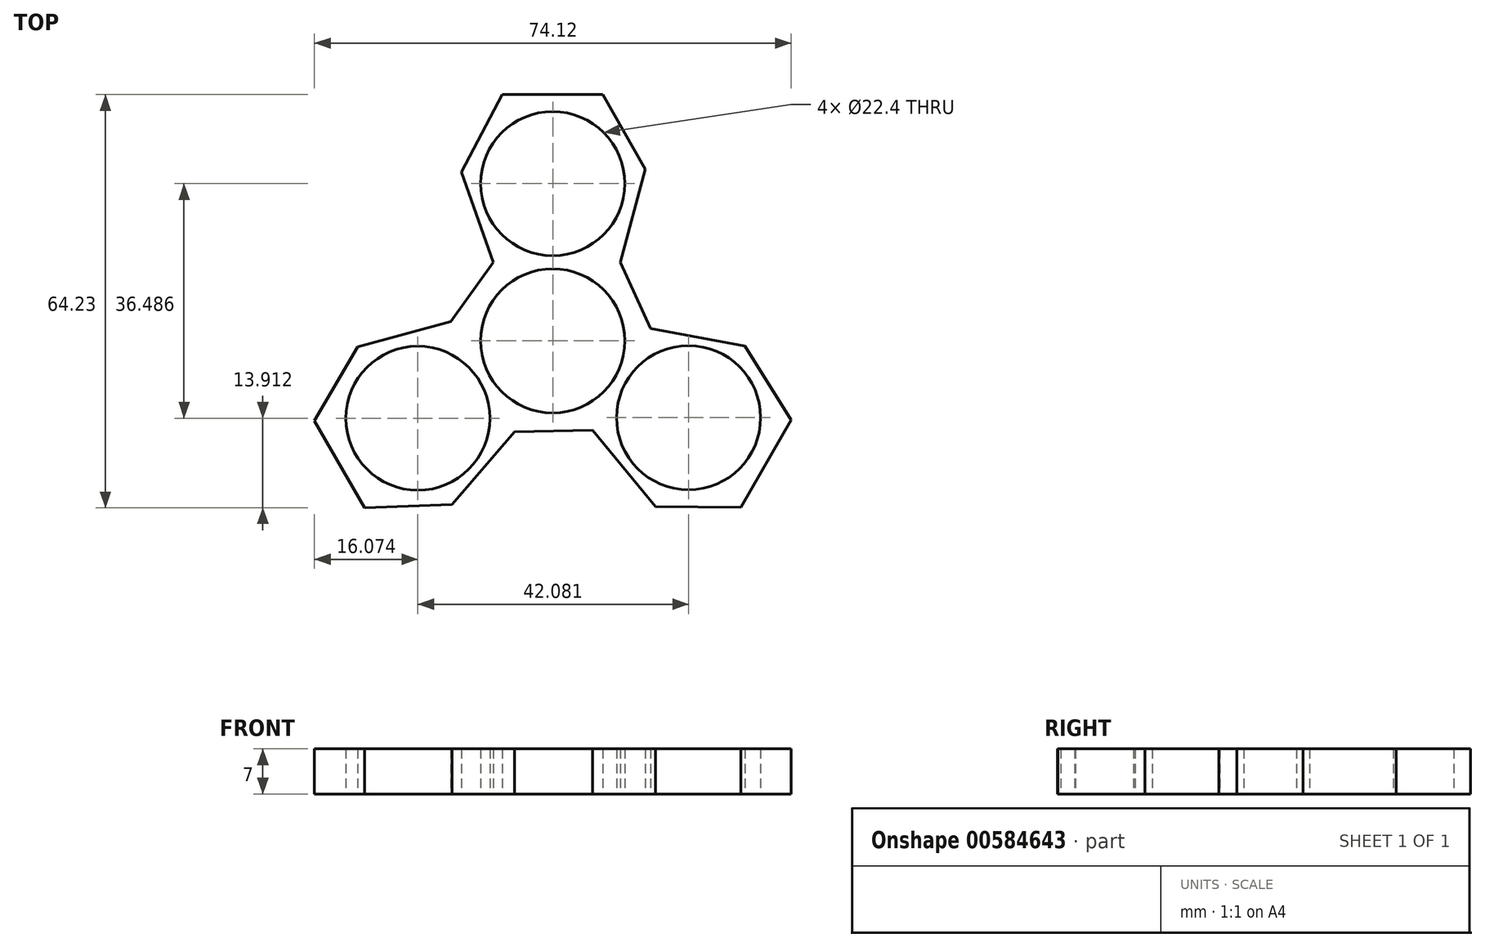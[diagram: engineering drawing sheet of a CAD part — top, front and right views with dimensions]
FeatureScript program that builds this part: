
annotation { "Feature Type Name" : "Feature", "Feature Type Description" : "" }
export const myFeature = defineFeature(function(context is Context, id is Id, definition is map)
    precondition{}
    {
        {
            var Q0;
            Q0=qCreatedBy(makeId("Top.planeOp"),FACE);
            var sketch = newSketch(context, id + "F0", { "sketchPlane" : qUnion([Q0])});
            skPoint(sketch, "E0.center", {"position": v(0, 0) * mm});
            skPoint(sketch, "E1.orphan", {"position": v(-15.95, 24.45) * mm});
            skPoint(sketch, "E2.2.0.center.orphan", {"position": v(0, 24.45) * mm});
            skPoint(sketch, "E3.orphan", {"position": v(15.54, 24.45) * mm});
            skCircle(sketch, "E4", {"center": v(0, 0) * mm, "radius": 11.2 * mm});
            skCircle(sketch, "E5", {"center": v(0, 24.45) * mm, "radius": 11.2 * mm});
            skCircle(sketch, "E6.1.0", {"center": v(-20.97, -12.04) * mm, "radius": 11.2 * mm});
            skCircle(sketch, "E6.2.0", {"center": v(21.12, -11.95) * mm, "radius": 11.2 * mm});
            skPoint(sketch, "E6.center", {"position": v(0.05, 0.15) * mm});
            skLineSegment(sketch, "E7", {"start": v(-7.86, 38.28) * mm, "end": v(7.78, 38.28) * mm});
            skLineSegment(sketch, "E8", {"start": v(7.78, 38.28) * mm, "end": v(14.35, 26.72) * mm});
            skLineSegment(sketch, "E9", {"start": v(14.35, 26.72) * mm, "end": v(10.5, 12.2) * mm});
            skLineSegment(sketch, "E10", {"start": v(-7.86, 38.28) * mm, "end": v(-14.21, 26.26) * mm});
            skLineSegment(sketch, "E11", {"start": v(-14.21, 26.26) * mm, "end": v(-9.26, 12.2) * mm});
            skLineSegment(sketch, "E12.1.0", {"start": v(29.85, -0.82) * mm, "end": v(15.2, 1.92) * mm});
            skLineSegment(sketch, "E12.1.2", {"start": v(29.26, -25.87) * mm, "end": v(15.96, -25.79) * mm});
            skLineSegment(sketch, "E12.1.3", {"start": v(37.08, -12.33) * mm, "end": v(29.26, -25.87) * mm});
            skLineSegment(sketch, "E12.1.4", {"start": v(37.08, -12.33) * mm, "end": v(29.85, -0.82) * mm});
            skLineSegment(sketch, "E12.2.0", {"start": v(-15.64, -25.44) * mm, "end": v(-5.94, -14.12) * mm});
            skLineSegment(sketch, "E12.2.1", {"start": v(-30.31, -0.93) * mm, "end": v(-15.82, 2.99) * mm});
            skLineSegment(sketch, "E12.2.2", {"start": v(-37.04, -12.4) * mm, "end": v(-30.31, -0.93) * mm});
            skLineSegment(sketch, "E12.2.3", {"start": v(-29.22, -25.95) * mm, "end": v(-37.04, -12.4) * mm});
            skLineSegment(sketch, "E12.2.4", {"start": v(-29.22, -25.95) * mm, "end": v(-15.64, -25.44) * mm});
            skLineSegment(sketch, "E12.anchor1", {"start": v(0, 0) * mm, "end": v(-9.26, 12.2) * mm, "construction": true});
            skLineSegment(sketch, "E13", {"start": v(-15.82, 2.99) * mm, "end": v(-9.26, 12.2) * mm});
            skLineSegment(sketch, "E14", {"start": v(15.96, -25.79) * mm, "end": v(6.2, -13.86) * mm});
            skLineSegment(sketch, "E15", {"start": v(-5.94, -14.12) * mm, "end": v(6.2, -13.86) * mm});
            skLineSegment(sketch, "E16", {"start": v(10.5, 12.2) * mm, "end": v(15.2, 1.92) * mm});
            skSolve(sketch);
        }
        {
            var Q0;
            Q0 = qSketchRegion(id + "F0", true);
            extrude(context, id + "F1", {"entities" : qUnion([Q0]), "depth" : 7 * mm, "offsetDistance" : 25 * mm});
        }
        {
            var Q0;
            Q0 = qSketchRegion(id + "F0", true);
            extrude(context, id + "F2", {"entities" : qUnion([Q0]), "operationType" : NewBodyOperationType.ADD, "depth" : 7 * mm, "offsetDistance" : 25 * mm});
        }
    });
